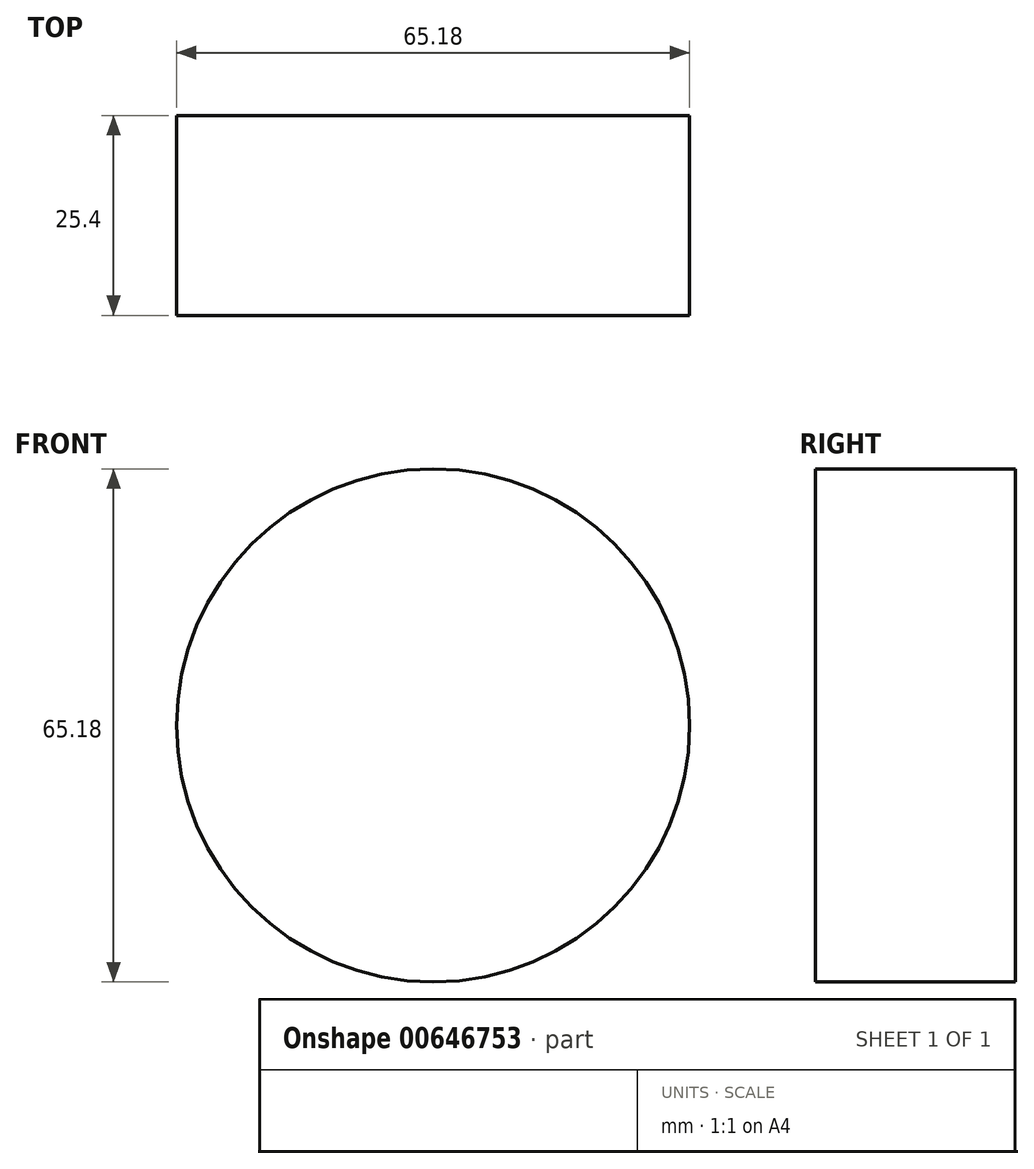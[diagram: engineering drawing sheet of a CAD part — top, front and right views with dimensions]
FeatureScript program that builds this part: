
annotation { "Feature Type Name" : "Feature", "Feature Type Description" : "" }
export const myFeature = defineFeature(function(context is Context, id is Id, definition is map)
    precondition{}
    {
        {
            var Q0;
            Q0=qCreatedBy(makeId("Front.planeOp"),FACE);
            var sketch = newSketch(context, id + "F0", { "sketchPlane" : qUnion([Q0])});
            skCircle(sketch, "E0", {"center": v(0, 0) * mm, "radius": 32.6 * mm});
            skSolve(sketch);
        }
        {
            var Q0;
            Q0 = qSketchRegion(id + "F0", true);
            var Q1;
            Q1=makeQuery(id+"F0.imprint","IMPRINT",FACE,{"disambiguationData":[TD([[makeQuery(id+"F0.imprint","IMPRINT",EDGE,{"derivedFrom":sQuery(id+"F0.wireOp",EDGE,"E0")}),1.0]])]});
            extrude(context, id + "F1", {"entities" : qUnion([Q0, Q1]), "depth" : 25.4 * mm, "offsetDistance" : 25.4 * mm});
        }
        {
            var Q0;
            Q0=qCreatedBy(makeId("Front.planeOp"),FACE);
            cPlane(context, id + "F2", {"entities" : qUnion([Q0]), "cplaneType" : CPlaneType.OFFSET, "offset" : 76.2 * mm, "width" : 152.4 * mm, "height" : 152.4 * mm});
        }
        {
            var Q0;
            Q0=qCreatedBy(id+"F2.planeOp",FACE);
            var sketch = newSketch(context, id + "F3", { "sketchPlane" : qUnion([Q0])});
            skLineSegment(sketch, "E1.bottom", {"start": v(-13.63, 21.44) * mm, "end": v(13.63, 21.44) * mm});
            skLineSegment(sketch, "E1.top", {"start": v(-13.63, -21.44) * mm, "end": v(13.63, -21.44) * mm});
            skLineSegment(sketch, "E1.left", {"start": v(-13.63, 21.44) * mm, "end": v(-13.63, -21.44) * mm});
            skLineSegment(sketch, "E1.right", {"start": v(13.63, 21.44) * mm, "end": v(13.63, -21.44) * mm});
            skPoint(sketch, "E1.middle", {"position": v(0, 0) * mm});
            skSolve(sketch);
        }
        {
            var Q0;
            Q0=makeQuery(id+"F1.opExtrude","CAP_EDGE",EDGE,{"disambiguationData":[OSD([sQuery(id+"F0.wireOp",EDGE,"E0")])],"isStart":false});
            var Q1;
            Q1=makeQuery(id+"F3.imprint","IMPRINT",FACE,{"disambiguationData":[TD([[makeQuery(id+"F3.imprint","IMPRINT",EDGE,{"derivedFrom":sQuery(id+"F3.wireOp",EDGE,"E1.bottom")}),-1.0]])]});
            loft(context, id + "F4", {"bodyType" : ToolBodyType.SURFACE, "wireProfilesArray" : [{ "wireProfileEntities" : qUnion([Q0]) }, { "wireProfileEntities" : qUnion([Q1]) }]});
        }
    });
